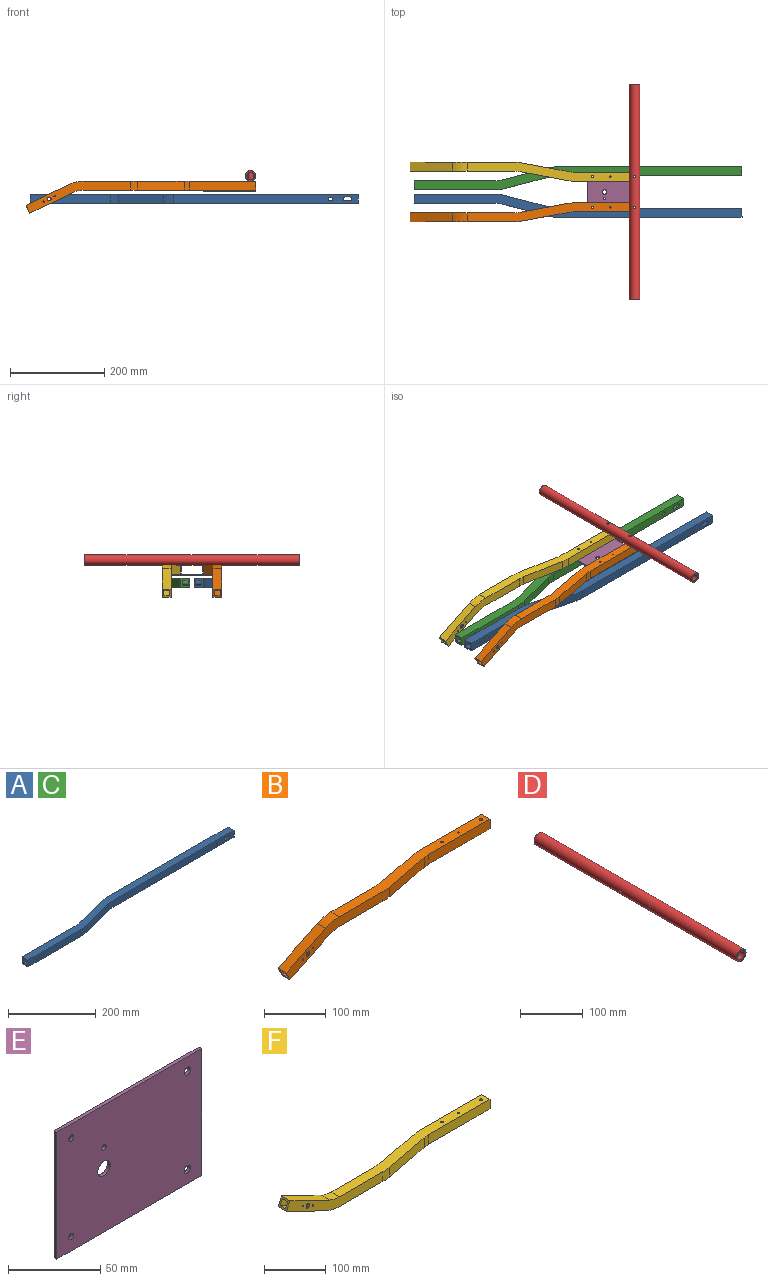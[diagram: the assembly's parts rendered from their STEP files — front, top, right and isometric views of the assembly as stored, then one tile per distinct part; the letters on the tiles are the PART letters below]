
ASSEMBLY  parts=6 mates=5
PART A: 54 faces, bbox 694.5x49.1x19.1 mm
  f0: plane 390x19.05mm, normal (0,1,0), area 7239.8mm2, adj f3,f5,f7,f12,f17,f18,f19,f20
  f1: plane 390x19.05mm, normal (0,-1,0), area 7239.8mm2, adj f3,f5,f7,f13,f17,f18,f19,f20
  f2: plane 19.05x19.05mm, normal (-1,0,0), area 205.4mm2, adj f4,f5,f6,f7,f28,f29,f30,f32
  f3: plane 19.05x19.05mm, normal (1,0,0), area 205.4mm2, adj f0,f1,f5,f7,f23,f24,f25,f26
  f4: plane 170x19.05mm, normal (0,1,0), area 3174.1mm2, adj f2,f5,f7,f8,f14,f15,f16
  f5: plane 694.54x49.05mm, normal (0,0,1), area 13300.1mm2, adj f0,f1,f2,f3,f4,f6,f8,f9
  f6: plane 170x19.05mm, normal (0,-1,0), area 3174.1mm2, adj f2,f5,f7,f9,f14,f15,f16
  f7: plane 694.54x49.05mm, normal (0,0,-1), area 13300.1mm2, adj f0,f1,f2,f3,f4,f6,f8,f9
  f8: cylinder r=65.48mm len=19.05mm, axis (0,0,1), area 317.4mm2, adj f4,f5,f7,f10
  f9: cylinder r=84.53mm len=21.28mm, axis (0,0,1), area 409.7mm2, adj f5,f6,f7,f11
  f10: plane 96.78x25.17mm, normal (-0.25,0.97,0), area 1905mm2, adj f5,f7,f8,f12
  f11: plane 96.78x25.17mm, normal (0.25,-0.97,0), area 1905mm2, adj f5,f7,f9,f13
  f12: cylinder r=84.53mm len=21.28mm, axis (0,0,-1), area 409.7mm2, adj f0,f5,f7,f10
  f13: cylinder r=65.48mm len=19.05mm, axis (0,0,-1), area 317.4mm2, adj f1,f5,f7,f11
  f14: cylinder r=4mm len=19.05mm, axis (0,-1,0), area 478.8mm2, adj f4,f6
  f15: cylinder r=1.5mm len=19.05mm, axis (0,-1,0), area 179.5mm2, adj f4,f6
  f16: cylinder r=1.5mm len=19.05mm, axis (0,-1,0), area 179.5mm2, adj f4,f6
  f17: cylinder r=4mm len=19.05mm, axis (0,-1,0), area 478.8mm2, adj f0,f1
  f18: plane 19.05x10mm, normal (0,0,-1), area 190.5mm2, adj f0,f1,f19,f21
  f19: cylinder r=4.2mm len=19.05mm, axis (0,-1,0), area 251.4mm2, adj f0,f1,f18,f20
  f20: plane 19.05x10mm, normal (0,0,1), area 190.5mm2, adj f0,f1,f19,f21
  f21: cylinder r=4.2mm len=19.05mm, axis (0,-1,0), area 251.4mm2, adj f0,f1,f18,f20
  f22: cylinder r=7.45mm len=12.55mm, axis (0,-1,0), area 187.3mm2, adj f23,f24,f25,f26
  f23: plane 13.28x12.55mm, normal (0,-1,0), area 136.3mm2, adj f3,f22,f25,f26
  f24: plane 13.28x12.55mm, normal (0,1,0), area 136.3mm2, adj f3,f22,f25,f26
  f25: plane 13.28x12.55mm, normal (0,0,1), area 166.7mm2, adj f3,f22,f23,f24
  f26: plane 13.28x12.55mm, normal (0,0,-1), area 166.7mm2, adj f3,f22,f23,f24
  f27: cylinder r=4.75mm len=12.55mm, axis (0,-1,0), area 374.6mm2, adj f28,f29
  f28: plane 36.37x12.55mm, normal (0,1,0), area 353.3mm2, adj f2,f27,f30,f31,f32
  f29: plane 36.37x12.55mm, normal (0,-1,0), area 353.3mm2, adj f2,f27,f30,f31,f32
  f30: plane 36.37x12.55mm, normal (0,0,1), area 456.4mm2, adj f2,f28,f29,f31
  f31: cylinder r=7.25mm len=12.55mm, axis (0,-1,0), area 190.4mm2, adj f28,f29,f30,f32
  f32: plane 36.37x12.55mm, normal (0,0,-1), area 456.4mm2, adj f2,f28,f29,f31
  f33: plane 23.41x12.55mm, normal (0,1,0), area 231.2mm2, adj f35,f36,f37,f38
  f34: plane 23.41x12.55mm, normal (0,-1,0), area 231.2mm2, adj f35,f36,f37,f38
  f35: plane 23.41x12.55mm, normal (0,0,-1), area 293.8mm2, adj f33,f34,f37,f38
  f36: plane 23.41x12.55mm, normal (0,0,1), area 293.8mm2, adj f33,f34,f37,f38
  f37: cylinder r=7.25mm len=12.55mm, axis (0,-1,0), area 190.4mm2, adj f33,f34,f35,f36
  f38: cylinder r=7.45mm len=12.55mm, axis (0,-1,0), area 187.3mm2, adj f33,f34,f35,f36
  f39: cylinder r=4.75mm len=12.55mm, axis (0,-1,0), area 374.6mm2, adj f49,f50
  f40: cylinder r=7.25mm len=12.55mm, axis (0,-1,0), area 190.4mm2, adj f49,f50,f51,f53
  f41: cylinder r=68.72mm len=17.3mm, axis (0,0,-1), area 219.5mm2, adj f43,f47,f51,f53
  f42: cylinder r=81.28mm len=20.46mm, axis (0,0,-1), area 259.5mm2, adj f44,f48,f51,f53
  f43: plane 96.78x25.17mm, normal (-0.25,0.97,0), area 1255mm2, adj f41,f45,f51,f53
  f44: plane 96.78x25.17mm, normal (0.25,-0.97,0), area 1255mm2, adj f42,f46,f51,f53
  f45: cylinder r=81.28mm len=20.46mm, axis (0,0,1), area 259.5mm2, adj f43,f50,f51,f53
  f46: cylinder r=68.72mm len=17.3mm, axis (0,0,1), area 219.5mm2, adj f44,f49,f51,f53
  f47: plane 328.01x12.55mm, normal (0,1,0), area 4084.3mm2, adj f41,f51,f52,f53
  f48: plane 328.01x12.55mm, normal (0,-1,0), area 4084.3mm2, adj f42,f51,f52,f53
  f49: plane 126.37x12.55mm, normal (0,-1,0), area 1482.8mm2, adj f39,f40,f46,f51,f53
  f50: plane 126.37x12.55mm, normal (0,1,0), area 1482.8mm2, adj f39,f40,f45,f51,f53
  f51: plane 588.91x42.55mm, normal (0,0,1), area 7436.4mm2, adj f40,f41,f42,f43,f44,f45,f46,f47
  f52: cylinder r=7.25mm len=12.55mm, axis (0,-1,0), area 190.4mm2, adj f47,f48,f51,f53
  f53: plane 588.91x42.55mm, normal (0,0,-1), area 7436.4mm2, adj f40,f41,f42,f43,f44,f45,f46,f47
PART B: 46 faces, bbox 487.1x40.1x68.1 mm
  f0: plane 19.05x19.05mm, normal (1,0,0), area 205.4mm2, adj f2,f3,f4,f5,f18,f19,f20,f21
  f1: plane 19.05x17.13mm, normal (-0.9,0,-0.44), area 205.4mm2, adj f12,f13,f16,f17,f28,f29,f32,f33
  f2: plane 140x19.05mm, normal (0,-1,0), area 2667mm2, adj f0,f3,f5,f6
  f3: plane 365.93x40.05mm, normal (0,0,1), area 6967.4mm2, adj f0,f2,f4,f6,f7,f8,f9,f10
  f4: plane 140x19.05mm, normal (0,1,0), area 2667mm2, adj f0,f3,f5,f7
  f5: plane 365.93x40.05mm, normal (0,0,-1), area 6967.4mm2, adj f0,f2,f4,f6,f7,f8,f9,f10
  f6: cylinder r=65.48mm len=19.05mm, axis (0,0,1), area 231.2mm2, adj f2,f3,f5,f8
  f7: cylinder r=84.53mm len=19.05mm, axis (0,0,1), area 298.5mm2, adj f3,f4,f5,f9
  f8: plane 98.29x19.05mm, normal (0.18,-0.98,0), area 1905mm2, adj f3,f5,f6,f10
  f9: plane 98.29x19.05mm, normal (-0.18,0.98,0), area 1905mm2, adj f3,f5,f7,f11
  f10: cylinder r=84.53mm len=19.05mm, axis (0,0,-1), area 298.5mm2, adj f3,f5,f8,f12
  f11: cylinder r=65.48mm len=19.05mm, axis (0,0,-1), area 231.2mm2, adj f3,f5,f9,f13
  f12: plane 221.14x68.09mm, normal (0,-1,0), area 4279mm2, adj f1,f3,f5,f10,f14,f15,f16,f17
  f13: plane 221.14x68.09mm, normal (0,1,0), area 4279mm2, adj f1,f3,f5,f11,f14,f15,f16,f17
  f14: cylinder r=71.34mm len=31.22mm, axis (0,-1,0), area 615.6mm2, adj f3,f12,f13,f16
  f15: cylinder r=52.29mm len=22.89mm, axis (0,-1,0), area 451.2mm2, adj f5,f12,f13,f17
  f16: plane 89.91x43.77mm, normal (-0.44,0,0.9), area 1905mm2, adj f1,f12,f13,f14
  f17: plane 89.91x43.77mm, normal (0.44,0,-0.9), area 1905mm2, adj f1,f12,f13,f15
  f18: plane 140x12.55mm, normal (0,1,0), area 1757mm2, adj f0,f19,f21,f22
  f19: plane 365.93x33.55mm, normal (0,0,-1), area 4576.7mm2, adj f0,f18,f20,f22,f23,f24,f25,f26
  f20: plane 140x12.55mm, normal (0,-1,0), area 1757mm2, adj f0,f19,f21,f23
  f21: plane 365.93x33.55mm, normal (0,0,1), area 4576.7mm2, adj f0,f18,f20,f22,f23,f24,f25,f26
  f22: cylinder r=68.72mm len=12.67mm, axis (0,0,1), area 159.9mm2, adj f18,f19,f21,f24
  f23: cylinder r=81.28mm len=14.98mm, axis (0,0,1), area 189.1mm2, adj f19,f20,f21,f25
  f24: plane 98.29x18.43mm, normal (-0.18,0.98,0), area 1255mm2, adj f19,f21,f22,f26
  f25: plane 98.29x18.43mm, normal (0.18,-0.98,0), area 1255mm2, adj f19,f21,f23,f27
  f26: cylinder r=81.28mm len=14.98mm, axis (0,0,-1), area 189.1mm2, adj f19,f21,f24,f28
  f27: cylinder r=68.72mm len=12.67mm, axis (0,0,-1), area 159.9mm2, adj f19,f21,f25,f29
  f28: plane 219.71x61.92mm, normal (0,1,0), area 2797mm2, adj f1,f19,f21,f26,f30,f31,f32,f33
  f29: plane 219.71x61.92mm, normal (0,-1,0), area 2797mm2, adj f1,f19,f21,f27,f30,f31,f32,f33
  f30: cylinder r=68.09mm len=29.8mm, axis (0,-1,0), area 387.1mm2, adj f19,f28,f29,f32
  f31: cylinder r=55.54mm len=24.31mm, axis (0,-1,0), area 315.8mm2, adj f21,f28,f29,f33
  f32: plane 89.91x43.77mm, normal (0.44,0,-0.9), area 1255mm2, adj f1,f28,f29,f30
  f33: plane 89.91x43.77mm, normal (-0.44,0,0.9), area 1255mm2, adj f1,f28,f29,f31
  f34: cylinder r=2mm len=4mm, axis (0,0,1), area 40.8mm2, adj f5,f21
  f35: cylinder r=1.5mm len=3.25mm, axis (0,0,1), area 30.6mm2, adj f5,f21
  f36: cylinder r=2.5mm len=5mm, axis (0,0,1), area 51.1mm2, adj f5,f21
  f37: cylinder r=2mm len=4mm, axis (0,0,1), area 40.8mm2, adj f3,f19
  f38: cylinder r=1.5mm len=3.25mm, axis (0,0,1), area 30.6mm2, adj f3,f19
  f39: cylinder r=2.5mm len=5mm, axis (0,0,1), area 51.1mm2, adj f3,f19
  f40: cylinder r=4mm len=8mm, axis (0,-1,0), area 81.7mm2, adj f13,f29
  f41: cylinder r=1.5mm len=3.25mm, axis (0,-1,0), area 30.6mm2, adj f13,f29
  f42: cylinder r=1.5mm len=3.25mm, axis (0,-1,0), area 30.6mm2, adj f13,f29
  f43: cylinder r=4mm len=8mm, axis (0,-1,0), area 81.7mm2, adj f12,f28
  f44: cylinder r=1.5mm len=3.25mm, axis (0,-1,0), area 30.6mm2, adj f12,f28
  f45: cylinder r=1.5mm len=3.25mm, axis (0,-1,0), area 30.6mm2, adj f12,f28
PART C: same geometry as A
PART D: 8 faces, bbox 22.2x455x22.2 mm
  f0: cylinder r=11.11mm len=455mm, axis (0,1,0), area 31682.9mm2, adj f1,f2,f3,f4
  f1: plane 22.22x22.22mm, normal (0,-1,0), area 193.7mm2, adj f0,f5
  f2: plane 22.22x22.22mm, normal (0,1,0), area 193.7mm2, adj f0,f5
  f3: cylinder r=2.5mm len=22.22mm, axis (1,0,0), area 344.6mm2, adj f0
  f4: cylinder r=2.5mm len=22.22mm, axis (1,0,0), area 344.6mm2, adj f0
  f5: cylinder r=7.86mm len=455mm, axis (0,1,0), area 22019.7mm2, adj f1,f2,f6,f7
  f6: cylinder r=5.75mm len=15.72mm, axis (1,0,0), area 481.9mm2, adj f5
  f7: cylinder r=5.75mm len=15.72mm, axis (1,0,0), area 481.9mm2, adj f5
PART E: 12 faces, bbox 111x2x84.4 mm
  f0: plane 84.37x2mm, normal (-1,0,0), area 168.7mm2, adj f1,f8,f10,f11
  f1: plane 111x2mm, normal (0,0,-1), area 222mm2, adj f0,f2,f10,f11
  f2: plane 84.37x2mm, normal (1,0,0), area 168.7mm2, adj f1,f8,f10,f11
  f3: cylinder r=4.75mm len=9.5mm, axis (0,1,0), area 59.7mm2, adj f10,f11
  f4: cylinder r=2mm len=4mm, axis (0,1,0), area 25.1mm2, adj f10,f11
  f5: cylinder r=2mm len=4mm, axis (0,1,0), area 25.1mm2, adj f10,f11
  f6: cylinder r=2.5mm len=5mm, axis (0,1,0), area 31.4mm2, adj f10,f11
  f7: cylinder r=2.5mm len=5mm, axis (0,1,0), area 31.4mm2, adj f10,f11
  f8: plane 111x2mm, normal (0,0,1), area 222mm2, adj f0,f2,f10,f11
  f9: cylinder r=1.75mm len=3.5mm, axis (0,1,0), area 22mm2, adj f10,f11
  f10: plane 111x84.37mm, normal (0,-1,0), area 9220.2mm2, adj f0,f1,f2,f3,f4,f5,f6,f7
  f11: plane 111x84.37mm, normal (0,1,0), area 9220.2mm2, adj f0,f1,f2,f3,f4,f5,f6,f7
PART F: 46 faces, bbox 487.1x40.1x68.1 mm
  f0: plane 19.05x19.05mm, normal (1,0,0), area 205.4mm2, adj f2,f3,f4,f5,f18,f19,f20,f21
  f1: plane 19.05x17.13mm, normal (-0.9,0,0.44), area 205.4mm2, adj f12,f13,f16,f17,f28,f29,f32,f33
  f2: plane 140x19.05mm, normal (0,-1,0), area 2667mm2, adj f0,f3,f5,f6
  f3: plane 365.93x40.05mm, normal (0,0,-1), area 6967.4mm2, adj f0,f2,f4,f6,f7,f8,f9,f10
  f4: plane 140x19.05mm, normal (0,1,0), area 2667mm2, adj f0,f3,f5,f7
  f5: plane 365.93x40.05mm, normal (0,0,1), area 6967.4mm2, adj f0,f2,f4,f6,f7,f8,f9,f10
  f6: cylinder r=65.48mm len=19.05mm, axis (0,0,-1), area 231.2mm2, adj f2,f3,f5,f8
  f7: cylinder r=84.53mm len=19.05mm, axis (0,0,-1), area 298.5mm2, adj f3,f4,f5,f9
  f8: plane 98.29x19.05mm, normal (0.18,-0.98,0), area 1905mm2, adj f3,f5,f6,f10
  f9: plane 98.29x19.05mm, normal (-0.18,0.98,0), area 1905mm2, adj f3,f5,f7,f11
  f10: cylinder r=84.53mm len=19.05mm, axis (0,0,1), area 298.5mm2, adj f3,f5,f8,f12
  f11: cylinder r=65.48mm len=19.05mm, axis (0,0,1), area 231.2mm2, adj f3,f5,f9,f13
  f12: plane 221.14x68.09mm, normal (0,-1,0), area 4279mm2, adj f1,f3,f5,f10,f14,f15,f16,f17
  f13: plane 221.14x68.09mm, normal (0,1,0), area 4279mm2, adj f1,f3,f5,f11,f14,f15,f16,f17
  f14: cylinder r=71.34mm len=31.22mm, axis (0,-1,0), area 615.6mm2, adj f3,f12,f13,f16
  f15: cylinder r=52.29mm len=22.89mm, axis (0,-1,0), area 451.2mm2, adj f5,f12,f13,f17
  f16: plane 89.91x43.77mm, normal (-0.44,0,-0.9), area 1905mm2, adj f1,f12,f13,f14
  f17: plane 89.91x43.77mm, normal (0.44,0,0.9), area 1905mm2, adj f1,f12,f13,f15
  f18: plane 140x12.55mm, normal (0,1,0), area 1757mm2, adj f0,f19,f21,f22
  f19: plane 365.93x33.55mm, normal (0,0,1), area 4576.7mm2, adj f0,f18,f20,f22,f23,f24,f25,f26
  f20: plane 140x12.55mm, normal (0,-1,0), area 1757mm2, adj f0,f19,f21,f23
  f21: plane 365.93x33.55mm, normal (0,0,-1), area 4576.7mm2, adj f0,f18,f20,f22,f23,f24,f25,f26
  f22: cylinder r=68.72mm len=12.67mm, axis (0,0,-1), area 159.9mm2, adj f18,f19,f21,f24
  f23: cylinder r=81.28mm len=14.98mm, axis (0,0,-1), area 189.1mm2, adj f19,f20,f21,f25
  f24: plane 98.29x18.43mm, normal (-0.18,0.98,0), area 1255mm2, adj f19,f21,f22,f26
  f25: plane 98.29x18.43mm, normal (0.18,-0.98,0), area 1255mm2, adj f19,f21,f23,f27
  f26: cylinder r=81.28mm len=14.98mm, axis (0,0,1), area 189.1mm2, adj f19,f21,f24,f28
  f27: cylinder r=68.72mm len=12.67mm, axis (0,0,1), area 159.9mm2, adj f19,f21,f25,f29
  f28: plane 219.71x61.92mm, normal (0,1,0), area 2797mm2, adj f1,f19,f21,f26,f30,f31,f32,f33
  f29: plane 219.71x61.92mm, normal (0,-1,0), area 2797mm2, adj f1,f19,f21,f27,f30,f31,f32,f33
  f30: cylinder r=68.09mm len=29.8mm, axis (0,-1,0), area 387.1mm2, adj f19,f28,f29,f32
  f31: cylinder r=55.54mm len=24.31mm, axis (0,-1,0), area 315.8mm2, adj f21,f28,f29,f33
  f32: plane 89.91x43.77mm, normal (0.44,0,0.9), area 1255mm2, adj f1,f28,f29,f30
  f33: plane 89.91x43.77mm, normal (-0.44,0,-0.9), area 1255mm2, adj f1,f28,f29,f31
  f34: cylinder r=2mm len=4mm, axis (0,0,-1), area 40.8mm2, adj f5,f21
  f35: cylinder r=1.5mm len=3.25mm, axis (0,0,-1), area 30.6mm2, adj f5,f21
  f36: cylinder r=2.5mm len=5mm, axis (0,0,-1), area 51.1mm2, adj f5,f21
  f37: cylinder r=2mm len=4mm, axis (0,0,-1), area 40.8mm2, adj f3,f19
  f38: cylinder r=1.5mm len=3.25mm, axis (0,0,-1), area 30.6mm2, adj f3,f19
  f39: cylinder r=2.5mm len=5mm, axis (0,0,-1), area 51.1mm2, adj f3,f19
  f40: cylinder r=4mm len=8mm, axis (0,-1,0), area 81.7mm2, adj f13,f29
  f41: cylinder r=1.5mm len=3.25mm, axis (0,-1,0), area 30.6mm2, adj f13,f29
  f42: cylinder r=1.5mm len=3.25mm, axis (0,-1,0), area 30.6mm2, adj f13,f29
  f43: cylinder r=4mm len=8mm, axis (0,-1,0), area 81.7mm2, adj f12,f28
  f44: cylinder r=1.5mm len=3.25mm, axis (0,-1,0), area 30.6mm2, adj f12,f28
  f45: cylinder r=1.5mm len=3.25mm, axis (0,-1,0), area 30.6mm2, adj f12,f28
PLACE A rot(axis=(-1,0,0),180deg) t=(-239.34,26.44,47.25)mm
PLACE B rot(axis=(0.92,-0.4,0.03),0deg) t=(-127.33,-13.22,75.37)mm
PLACE C t=(-239.34,54.49,47.25)mm fixed
PLACE D rot(axis=(0,1,0),90deg) t=(227.6,267.96,96.14)mm
PLACE E rot(axis=(1,0,0),90deg) t=(127.6,82.65,65.85)mm
PLACE F rot(axis=(-1,0,0),180deg) t=(-127.33,94.15,94.42)mm
MATE fastened B.f36 <-> E.f6  axis (0,0,-1) through (227.6,7.78,65.85)mm
MATE fastened B.f36 <-> D.f3  axis (0,0,1) through (227.6,7.78,84.9)mm
MATE fastened A.f14 <-> C.f14  axis (0,1,0) through (-199.34,35.96,47.25)mm
MATE fastened E.f7 <-> F.f36  axis (0,0,1) through (227.6,73.15,65.85)mm
MATE revolute B.f40 <-> A.f14  axis (0,1,0) through (-199.34,-3.7,47.25)mm
